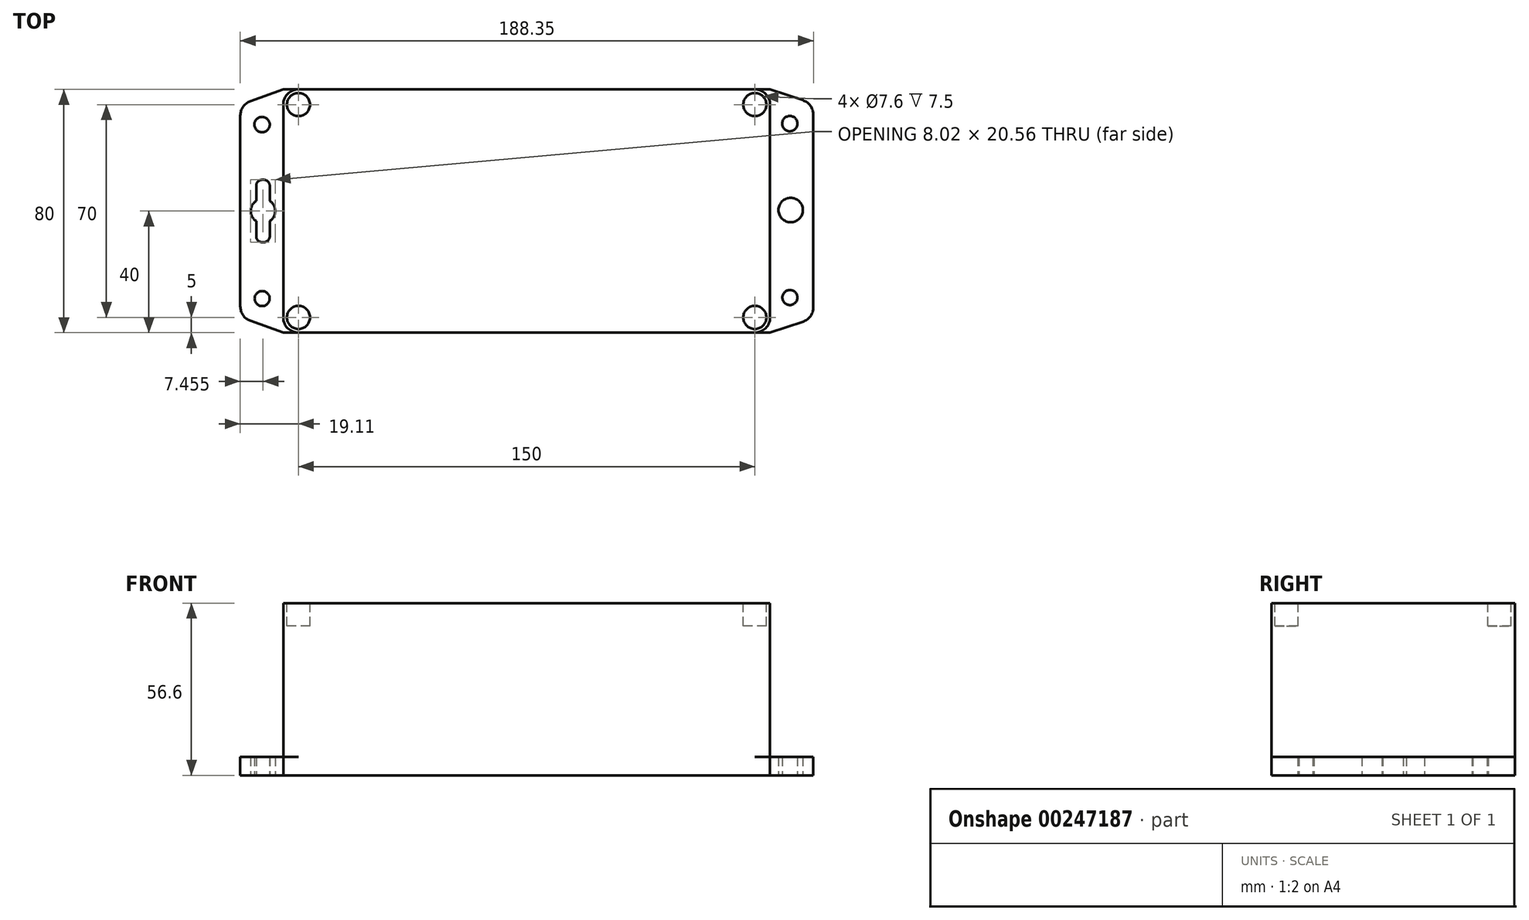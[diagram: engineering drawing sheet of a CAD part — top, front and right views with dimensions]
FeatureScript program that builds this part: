
annotation { "Feature Type Name" : "Feature", "Feature Type Description" : "" }
export const myFeature = defineFeature(function(context is Context, id is Id, definition is map)
    precondition{}
    {
        {
            var Q0;
            Q0=qCreatedBy(makeId("Top.planeOp"),FACE);
            var sketch = newSketch(context, id + "F0", { "sketchPlane" : qUnion([Q0])});
            skLineSegment(sketch, "E0.bottom", {"start": v(75, 40) * mm, "end": v(-75, 40) * mm});
            skLineSegment(sketch, "E0.top", {"start": v(75, -40) * mm, "end": v(-75, -40) * mm});
            skLineSegment(sketch, "E0.left", {"start": v(80, 35) * mm, "end": v(80, -35) * mm});
            skLineSegment(sketch, "E0.right", {"start": v(-80, 35) * mm, "end": v(-80, -35) * mm});
            skPoint(sketch, "E0.middle", {"position": v(0, 0) * mm});
            skLineSegment(sketch, "E1", {"start": v(-80, -40) * mm, "end": v(-90.8, -36.1) * mm});
            skLineSegment(sketch, "E2", {"start": v(-94.1, -31.4) * mm, "end": v(-94.1, 31.4) * mm});
            skLineSegment(sketch, "E3", {"start": v(-90.8, 36.1) * mm, "end": v(-80, 40) * mm});
            skLineSegment(sketch, "E4", {"start": v(80, 40) * mm, "end": v(90.81, 36.41) * mm});
            skLineSegment(sketch, "E5", {"start": v(94.24, 31.67) * mm, "end": v(94.24, -31.67) * mm});
            skLineSegment(sketch, "E6", {"start": v(90.81, -36.41) * mm, "end": v(80, -40) * mm});
            skPoint(sketch, "E7.visualSharp", {"position": v(-94.1, 34.9) * mm});
            skArc(sketch, "E7.filletArc", {"start": v(-90.8, 36.1) * mm, "mid": v(-93.2, 34.26) * mm, "end": v(-94.1, 31.4) * mm});
            skPoint(sketch, "E8.visualSharp", {"position": v(-94.1, -34.9) * mm});
            skArc(sketch, "E8.filletArc", {"start": v(-94.1, -31.4) * mm, "mid": v(-93.2, -34.26) * mm, "end": v(-90.8, -36.1) * mm});
            skPoint(sketch, "E9.visualSharp", {"position": v(94.24, -35.28) * mm});
            skArc(sketch, "E9.filletArc", {"start": v(90.81, -36.41) * mm, "mid": v(93.3, -34.6) * mm, "end": v(94.24, -31.67) * mm});
            skPoint(sketch, "E10.visualSharp", {"position": v(94.24, 35.28) * mm});
            skArc(sketch, "E10.filletArc", {"start": v(94.24, 31.67) * mm, "mid": v(93.3, 34.6) * mm, "end": v(90.81, 36.41) * mm});
            skCircle(sketch, "E11", {"center": v(-86.95, 28.43) * mm, "radius": 2.52 * mm});
            skCircle(sketch, "E12", {"center": v(-86.93, -28.8) * mm, "radius": 2.47 * mm});
            skLineSegment(sketch, "E13.bottom", {"start": v(-86.43, -10.28) * mm, "end": v(-86.88, -10.28) * mm});
            skLineSegment(sketch, "E13.top", {"start": v(-86.43, 10.28) * mm, "end": v(-86.88, 10.28) * mm});
            skLineSegment(sketch, "E13.left", {"start": v(-84.43, -8.28) * mm, "end": v(-84.43, 8.28) * mm});
            skLineSegment(sketch, "E13.right", {"start": v(-88.88, -8.28) * mm, "end": v(-88.88, 8.28) * mm});
            skPoint(sketch, "E13.middle", {"position": v(-86.65, 0) * mm});
            skPoint(sketch, "E14.visualSharp", {"position": v(-88.88, 10.28) * mm});
            skArc(sketch, "E14.filletArc", {"start": v(-86.88, 10.28) * mm, "mid": v(-88.3, 9.7) * mm, "end": v(-88.88, 8.28) * mm});
            skPoint(sketch, "E15.visualSharp", {"position": v(-84.43, 10.28) * mm});
            skArc(sketch, "E15.filletArc", {"start": v(-84.43, 8.28) * mm, "mid": v(-85.01, 9.7) * mm, "end": v(-86.43, 10.28) * mm});
            skPoint(sketch, "E16.visualSharp", {"position": v(-84.43, -10.28) * mm});
            skArc(sketch, "E16.filletArc", {"start": v(-86.43, -10.28) * mm, "mid": v(-85.01, -9.7) * mm, "end": v(-84.43, -8.28) * mm});
            skPoint(sketch, "E17.visualSharp", {"position": v(-88.88, -10.28) * mm});
            skArc(sketch, "E17.filletArc", {"start": v(-88.88, -8.28) * mm, "mid": v(-88.3, -9.7) * mm, "end": v(-86.88, -10.28) * mm});
            skCircle(sketch, "E18", {"center": v(-86.65, 0) * mm, "radius": 4.01 * mm});
            skCircle(sketch, "E19", {"center": v(86.49, 28.75) * mm, "radius": 2.52 * mm});
            skCircle(sketch, "E20", {"center": v(86.51, -28.48) * mm, "radius": 2.47 * mm});
            skLineSegment(sketch, "E21.left", {"start": v(89.01, -7.96) * mm, "end": v(89.01, 8.6) * mm});
            skLineSegment(sketch, "E21.right", {"start": v(84.56, -7.96) * mm, "end": v(84.56, 8.6) * mm});
            skPoint(sketch, "E21.middle", {"position": v(86.79, 0.32) * mm});
            skArc(sketch, "E22.filletArc", {"start": v(86.56, 10.6) * mm, "mid": v(85.14, 10.01) * mm, "end": v(84.56, 8.6) * mm});
            skArc(sketch, "E23.filletArc", {"start": v(89.01, 8.6) * mm, "mid": v(88.43, 10.01) * mm, "end": v(87.01, 10.6) * mm});
            skArc(sketch, "E24.filletArc", {"start": v(87.01, -9.96) * mm, "mid": v(88.43, -9.37) * mm, "end": v(89.01, -7.96) * mm});
            skArc(sketch, "E25.filletArc", {"start": v(84.56, -7.96) * mm, "mid": v(85.14, -9.37) * mm, "end": v(86.56, -9.96) * mm});
            skCircle(sketch, "E26", {"center": v(86.79, 0.32) * mm, "radius": 4.01 * mm});
            skPoint(sketch, "E27.visualSharp", {"position": v(-80, 40) * mm});
            skArc(sketch, "E27.filletArc", {"start": v(-75, 40) * mm, "mid": v(-78.54, 38.54) * mm, "end": v(-80, 35) * mm});
            skPoint(sketch, "E28.visualSharp", {"position": v(-80, -40) * mm});
            skArc(sketch, "E28.filletArc", {"start": v(-80, -35) * mm, "mid": v(-78.54, -38.54) * mm, "end": v(-75, -40) * mm});
            skPoint(sketch, "E29.visualSharp", {"position": v(80, -40) * mm});
            skArc(sketch, "E29.filletArc", {"start": v(75, -40) * mm, "mid": v(78.54, -38.54) * mm, "end": v(80, -35) * mm});
            skPoint(sketch, "E30.visualSharp", {"position": v(80, 40) * mm});
            skArc(sketch, "E30.filletArc", {"start": v(80, 35) * mm, "mid": v(78.54, 38.54) * mm, "end": v(75, 40) * mm});
            skLineSegment(sketch, "E31", {"start": v(-80, 40) * mm, "end": v(-75, 40) * mm});
            skLineSegment(sketch, "E32", {"start": v(-80, -40) * mm, "end": v(-75, -40) * mm});
            skLineSegment(sketch, "E33", {"start": v(75, 40) * mm, "end": v(80, 40) * mm});
            skLineSegment(sketch, "E34", {"start": v(75, -40) * mm, "end": v(80, -40) * mm});
            skLineSegment(sketch, "E35", {"start": v(-65, 37.47) * mm, "end": v(0, 37.47) * mm});
            skLineSegment(sketch, "E36", {"start": v(0, 37.47) * mm, "end": v(65, 37.47) * mm});
            skLineSegment(sketch, "E37", {"start": v(0, -37.49) * mm, "end": v(65, -37.49) * mm});
            skLineSegment(sketch, "E38", {"start": v(0, -37.49) * mm, "end": v(-65, -37.49) * mm});
            skLineSegment(sketch, "E39", {"start": v(-68, 34.47) * mm, "end": v(-68, 22.47) * mm});
            skLineSegment(sketch, "E40", {"start": v(-68, -34.49) * mm, "end": v(-68, -22.55) * mm});
            skLineSegment(sketch, "E41", {"start": v(68, 34.47) * mm, "end": v(68, 22.47) * mm});
            skLineSegment(sketch, "E42", {"start": v(68, -34.49) * mm, "end": v(68, -22.49) * mm});
            skLineSegment(sketch, "E43", {"start": v(-71, 19.47) * mm, "end": v(-74.09, 19.47) * mm});
            skLineSegment(sketch, "E44", {"start": v(-77.09, 16.47) * mm, "end": v(-77.09, -16.6) * mm});
            skLineSegment(sketch, "E45", {"start": v(-74.03, -19.6) * mm, "end": v(-71.06, -19.55) * mm});
            skLineSegment(sketch, "E46", {"start": v(71, 19.47) * mm, "end": v(74.17, 19.47) * mm});
            skLineSegment(sketch, "E47", {"start": v(77.17, 16.47) * mm, "end": v(77.17, -16.49) * mm});
            skLineSegment(sketch, "E48", {"start": v(74.17, -19.49) * mm, "end": v(71, -19.49) * mm});
            skPoint(sketch, "E49.visualSharp", {"position": v(-68, 19.47) * mm});
            skArc(sketch, "E49.filletArc", {"start": v(-71, 19.47) * mm, "mid": v(-68.88, 20.35) * mm, "end": v(-68, 22.47) * mm});
            skPoint(sketch, "E50.visualSharp", {"position": v(-77.09, 19.47) * mm});
            skArc(sketch, "E50.filletArc", {"start": v(-74.09, 19.47) * mm, "mid": v(-76.2, 18.59) * mm, "end": v(-77.09, 16.47) * mm});
            skPoint(sketch, "E51.visualSharp", {"position": v(-77.09, -19.67) * mm});
            skArc(sketch, "E51.filletArc", {"start": v(-77.09, -16.6) * mm, "mid": v(-76.19, -18.75) * mm, "end": v(-74.03, -19.6) * mm});
            skPoint(sketch, "E52.visualSharp", {"position": v(-68, -19.49) * mm});
            skArc(sketch, "E52.filletArc", {"start": v(-68, -22.55) * mm, "mid": v(-68.9, -20.4) * mm, "end": v(-71.06, -19.55) * mm});
            skPoint(sketch, "E53.visualSharp", {"position": v(-68, -37.49) * mm});
            skArc(sketch, "E53.filletArc", {"start": v(-68, -34.49) * mm, "mid": v(-67.12, -36.6) * mm, "end": v(-65, -37.49) * mm});
            skPoint(sketch, "E54.visualSharp", {"position": v(68, -37.49) * mm});
            skArc(sketch, "E54.filletArc", {"start": v(65, -37.49) * mm, "mid": v(67.12, -36.6) * mm, "end": v(68, -34.49) * mm});
            skPoint(sketch, "E55.visualSharp", {"position": v(68, -19.49) * mm});
            skArc(sketch, "E55.filletArc", {"start": v(71, -19.49) * mm, "mid": v(68.88, -20.36) * mm, "end": v(68, -22.49) * mm});
            skPoint(sketch, "E56.visualSharp", {"position": v(77.17, -19.49) * mm});
            skArc(sketch, "E56.filletArc", {"start": v(74.17, -19.49) * mm, "mid": v(76.3, -18.6) * mm, "end": v(77.17, -16.49) * mm});
            skPoint(sketch, "E57.visualSharp", {"position": v(77.17, 19.47) * mm});
            skArc(sketch, "E57.filletArc", {"start": v(77.17, 16.47) * mm, "mid": v(76.3, 18.59) * mm, "end": v(74.17, 19.47) * mm});
            skPoint(sketch, "E58.visualSharp", {"position": v(68, 19.47) * mm});
            skArc(sketch, "E58.filletArc", {"start": v(68, 22.47) * mm, "mid": v(68.88, 20.35) * mm, "end": v(71, 19.47) * mm});
            skPoint(sketch, "E59.visualSharp", {"position": v(68, 37.47) * mm});
            skArc(sketch, "E59.filletArc", {"start": v(68, 34.47) * mm, "mid": v(67.12, 36.59) * mm, "end": v(65, 37.47) * mm});
            skPoint(sketch, "E60.visualSharp", {"position": v(-68, 37.47) * mm});
            skArc(sketch, "E60.filletArc", {"start": v(-65, 37.47) * mm, "mid": v(-67.12, 36.59) * mm, "end": v(-68, 34.47) * mm});
            skSolve(sketch);
        }
        {
            var Q0;
            Q0=makeQuery(id+"F0.imprint","IMPRINT",FACE,{"disambiguationData":[TD([[makeQuery(id+"F0.imprint","IMPRINT",EDGE,{"derivedFrom":sQuery(id+"F0.wireOp",EDGE,"E0.bottom")}),1.0]])]});
            var Q1;
            Q1=makeQuery(id+"F0.imprint","IMPRINT",FACE,{"disambiguationData":[TD([[makeQuery(id+"F0.imprint","IMPRINT",EDGE,{"derivedFrom":sQuery(id+"F0.wireOp",EDGE,"E0.left")}),1.0]])]});
            var Q2;
            Q2=makeQuery(id+"F0.imprint","IMPRINT",FACE,{"disambiguationData":[TD([[makeQuery(id+"F0.imprint","IMPRINT",EDGE,{"derivedFrom":sQuery(id+"F0.wireOp",EDGE,"E0.right")}),-1.0]])]});
            extrude(context, id + "F1", {"entities" : qUnion([Q0, Q1, Q2]), "depth" : 6 * mm});
        }
        {
            var Q0;
            Q0=makeQuery(id+"F0.imprint","IMPRINT",FACE,{"disambiguationData":[TD([[makeQuery(id+"F0.imprint","IMPRINT",EDGE,{"derivedFrom":sQuery(id+"F0.wireOp",EDGE,"E0.bottom")}),1.0]])]});
            extrude(context, id + "F2", {"entities" : qUnion([Q0]), "operationType" : NewBodyOperationType.ADD, "depth" : 34 * mm});
        }
        {
            var Q0;
            Q0=makeQuery(id+"F0.imprint","IMPRINT",FACE,{"disambiguationData":[TD([[makeQuery(id+"F0.imprint","IMPRINT",EDGE,{"derivedFrom":sQuery(id+"F0.wireOp",EDGE,"E35")}),-1.0]])]});
            var Q1;
            Q1=makeQuery(id+"F0.imprint","IMPRINT",FACE,{"disambiguationData":[TD([[makeQuery(id+"F0.imprint","IMPRINT",EDGE,{"derivedFrom":sQuery(id+"F0.wireOp",EDGE,"E0.bottom")}),1.0]])]});
            var Q2;
            Q2=makeQuery(id+"F0.imprint","IMPRINT",FACE,{"disambiguationData":[TD([[makeQuery(id+"F0.imprint","IMPRINT",EDGE,{"derivedFrom":sQuery(id+"F0.wireOp",EDGE,"E0.right")}),-1.0]])]});
            var Q3;
            Q3=makeQuery(id+"F0.imprint","IMPRINT",FACE,{"disambiguationData":[TD([[makeQuery(id+"F0.imprint","IMPRINT",EDGE,{"derivedFrom":sQuery(id+"F0.wireOp",EDGE,"E0.left")}),1.0]])]});
            extrude(context, id + "F3", {"entities" : qUnion([Q0, Q1, Q2, Q3]), "operationType" : NewBodyOperationType.ADD, "depth" : 6 * mm});
        }
        {
            var Q0;
            Q0=makeQuery(id+"F0.imprint","IMPRINT",FACE,{"disambiguationData":[TD([[makeQuery(id+"F0.imprint","IMPRINT",EDGE,{"derivedFrom":sQuery(id+"F0.wireOp",EDGE,"E0.bottom")}),1.0]])]});
            var Q1;
            Q1=makeQuery(id+"F0.imprint","IMPRINT",FACE,{"disambiguationData":[TD([[makeQuery(id+"F0.imprint","IMPRINT",EDGE,{"derivedFrom":sQuery(id+"F0.wireOp",EDGE,"E35")}),-1.0]])]});
            extrude(context, id + "F4", {"entities" : qUnion([Q0, Q1]), "operationType" : NewBodyOperationType.ADD, "depth" : 56.6 * mm});
        }
        {
            var Q0;
            Q0=makeQuery(id+"F4.opExtrude","CAP_FACE",FACE,{"disambiguationData":[OSD([sQuery(id+"F0.wireOp",EDGE,"E0.bottom"),sQuery(id+"F0.wireOp",EDGE,"E0.top"),sQuery(id+"F0.wireOp",EDGE,"E0.left"),sQuery(id+"F0.wireOp",EDGE,"E0.right"),sQuery(id+"F0.wireOp",EDGE,"E27.filletArc"),sQuery(id+"F0.wireOp",EDGE,"E28.filletArc"),sQuery(id+"F0.wireOp",EDGE,"E29.filletArc"),sQuery(id+"F0.wireOp",EDGE,"E30.filletArc")])],"isStart":false});
            var sketch = newSketch(context, id + "F5", { "sketchPlane" : qUnion([Q0])});
            skCircle(sketch, "E61", {"center": v(-75, 35) * mm, "radius": 3.8 * mm});
            skCircle(sketch, "E62", {"center": v(-75, -35) * mm, "radius": 3.8 * mm});
            skCircle(sketch, "E63", {"center": v(75, -35) * mm, "radius": 3.8 * mm});
            skCircle(sketch, "E64", {"center": v(75, 35) * mm, "radius": 3.8 * mm});
            skSolve(sketch);
        }
        {
            var Q0;
            Q0=makeQuery(id+"F5.imprint","IMPRINT",FACE,{"disambiguationData":[TD([[makeQuery(id+"F5.imprint","IMPRINT",EDGE,{"derivedFrom":sQuery(id+"F5.wireOp",EDGE,"E61")}),1.0]])]});
            var Q1;
            Q1=makeQuery(id+"F5.imprint","IMPRINT",FACE,{"disambiguationData":[TD([[makeQuery(id+"F5.imprint","IMPRINT",EDGE,{"derivedFrom":sQuery(id+"F5.wireOp",EDGE,"E62")}),1.0]])]});
            var Q2;
            Q2=makeQuery(id+"F5.imprint","IMPRINT",FACE,{"disambiguationData":[TD([[makeQuery(id+"F5.imprint","IMPRINT",EDGE,{"derivedFrom":sQuery(id+"F5.wireOp",EDGE,"E63")}),1.0]])]});
            var Q3;
            Q3=makeQuery(id+"F5.imprint","IMPRINT",FACE,{"disambiguationData":[TD([[makeQuery(id+"F5.imprint","IMPRINT",EDGE,{"derivedFrom":sQuery(id+"F5.wireOp",EDGE,"E64")}),1.0]])]});
            extrude(context, id + "F6", {"entities" : qUnion([Q0, Q1, Q2, Q3]), "operationType" : NewBodyOperationType.REMOVE, "oppositeDirection" : true, "depth" : 7.5 * mm});
        }
    });
